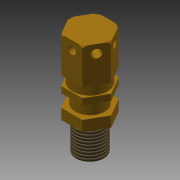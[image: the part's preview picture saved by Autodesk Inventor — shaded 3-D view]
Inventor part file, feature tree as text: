
AUTODESK INVENTOR PART (.ipt)
format: ipt  version: 2018 (Build 220112000, 112)  size: 202,752 bytes
history: native  units: mm (DEFAULTED — no unit token found)
features: sketch x9, projected_geometry x9, extrude x8, pattern_circular x1, thread x1, fillet x1, revolve x1
ambient origin geometry x8: Origin, YZ Plane, XZ Plane, XY Plane, X Axis, Y Axis, Z Axis, Center Point
bodies: Solid1 (feature_tree)
feature tree (30):
  extrude  "Extrusion1"  Depth=17.0mm TaperAngle=0.0deg
  extrude  "Extrusion2"  Depth=4.5mm TaperAngle=0.0deg
  extrude  "Extrusion3"  Depth=14.0mm
  extrude  "Extrusion4"  Depth=5.0mm TaperAngle=0.0deg
  extrude  "Extrusion5"  Depth=14.5mm TaperAngle=0.0deg
  extrude  "Extrusion6"  Depth=47.5mm TaperAngle=0.0deg
  extrude  "Extrusion7"  Depth=4.0mm
  extrude  "Extrusion8"  Depth=30.0mm TaperAngle=360.0deg
  pattern_circular  "Circular Pattern1"  Angle=45.0deg  [1 undecoded]
  thread  "Thread1"  [1 undecoded]
  fillet  "Fillet1"  [1 undecoded]
  revolve  "Revolution2"  [1 undecoded]
  sketch  "Sketch1"  dims[d0=17.5mm d1=17.0mm d2=0.0mm]
  sketch  "Sketch2"  dims[d3=16.5mm d4=4.5mm d5=0.0mm]
  projected_geometry  "Projected Loop1"
  sketch  "Sketch3"  dims[d6=3.0mm d7=0.0mm d8=14.0mm]
  projected_geometry  "Projected Loop2"
  sketch  "Sketch4"  dims[d9=6.0mm d10=0.0mm d11=5.0mm d12=0.0mm]
  projected_geometry  "Projected Loop3"
  sketch  "Sketch5"  dims[d13=13.25mm d14=14.5mm d15=0.0mm]
  projected_geometry  "Projected Loop4"
  sketch  "Sketch6"  dims[d16=5.0mm d17=47.5mm d18=0.0mm]
  projected_geometry  "Projected Loop5"
  sketch  "Sketch7"  dims[d19=4.0mm d20=4.0mm]
  projected_geometry  "Projected Loop6"
  sketch  "Sketch8"  dims[d21=40.25mm d22=0.0mm d23=30.0mm d25=360.0deg]
  projected_geometry  "Projected Loop7"
  sketch  "Sketch10"  dims[d26=10.0mm d27=0.0mm d28=0.5mm d32=45.0deg d33=1.0mm d34=90.0deg]
  projected_geometry  "Projected Loop8"
  projected_geometry  "Projected Loop9"
note: 4 required parameter values undecoded (feature->parameter linkage not recoverable at this tier; creation-order binding heuristic only, values carry confidence <= 0.55)
